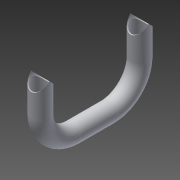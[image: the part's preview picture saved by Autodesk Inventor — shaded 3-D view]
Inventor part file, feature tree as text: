
AUTODESK INVENTOR PART (.ipt)
format: ipt  version: 2015 (Build 190159000, 159)  size: 180,224 bytes
history: native  units: mm
features: other x5, sketch x3, sweep x1, extrude x1
ambient origin geometry x8: Origin, YZ Plane, XZ Plane, XY Plane, X Axis, Y Axis, Z Axis, Center Point
bodies: Body1 (feature_tree)
feature tree (10):
  other  "Bryła1"
  other  "Płaszczyzna konstrukcyjna1"
  sketch  "Szkic1"
  other  "Płaszczyzna konstrukcyjna2"
  sweep  "Przeciągnięcie1"
  extrude  "Wyciągnięcie proste1"  Depth=1.5mm
  other  "Utwórz kombinację1"
  sketch  "Szkic2"
  sketch  "Szkic3"
  other  "Bryła2"
